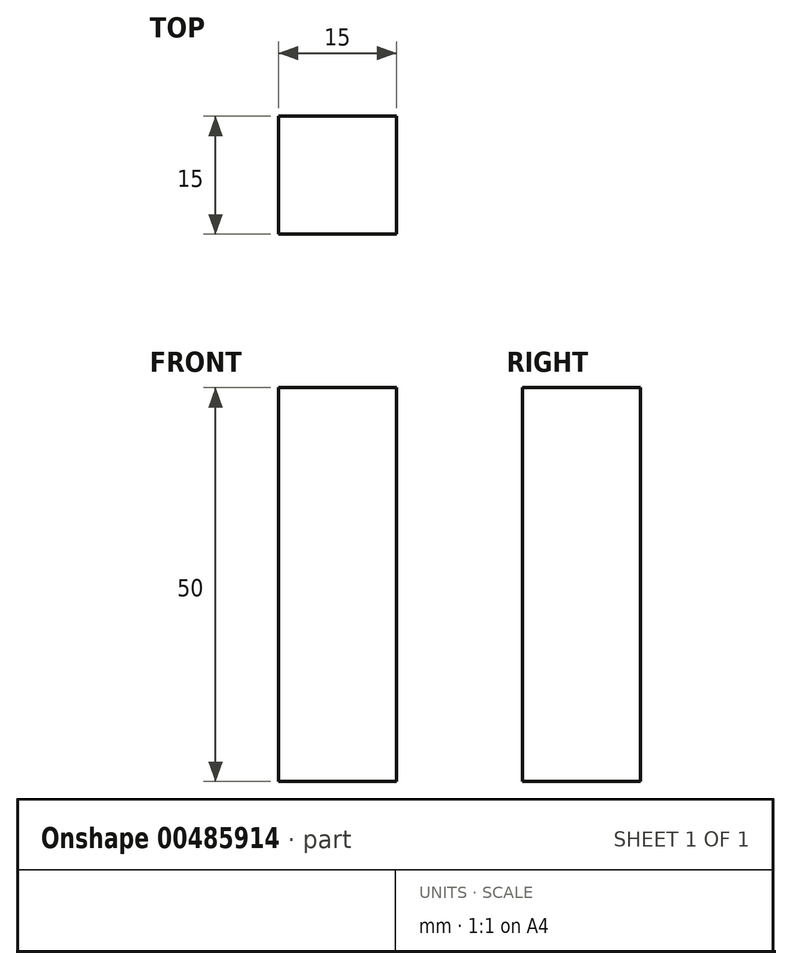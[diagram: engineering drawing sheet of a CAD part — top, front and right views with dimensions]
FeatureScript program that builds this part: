
annotation { "Feature Type Name" : "Feature", "Feature Type Description" : "" }
export const myFeature = defineFeature(function(context is Context, id is Id, definition is map)
    precondition{}
    {
        {
            var Q0;
            Q0=qCreatedBy(makeId("Top.planeOp"),FACE);
            var sketch = newSketch(context, id + "F0", { "sketchPlane" : qUnion([Q0])});
            skLineSegment(sketch, "E0.bottom", {"start": v(-7.5, 7.5) * mm, "end": v(7.5, 7.5) * mm});
            skLineSegment(sketch, "E0.top", {"start": v(-7.5, -7.5) * mm, "end": v(7.5, -7.5) * mm});
            skLineSegment(sketch, "E0.left", {"start": v(-7.5, 7.5) * mm, "end": v(-7.5, -7.5) * mm});
            skLineSegment(sketch, "E0.right", {"start": v(7.5, 7.5) * mm, "end": v(7.5, -7.5) * mm});
            skPoint(sketch, "E0.middle", {"position": v(0, 0) * mm});
            skSolve(sketch);
        }
        {
            var Q0;
            Q0 = qSketchRegion(id + "F0", true);
            extrude(context, id + "F1", {"entities" : qUnion([Q0]), "depth" : 50 * mm});
        }
    });
